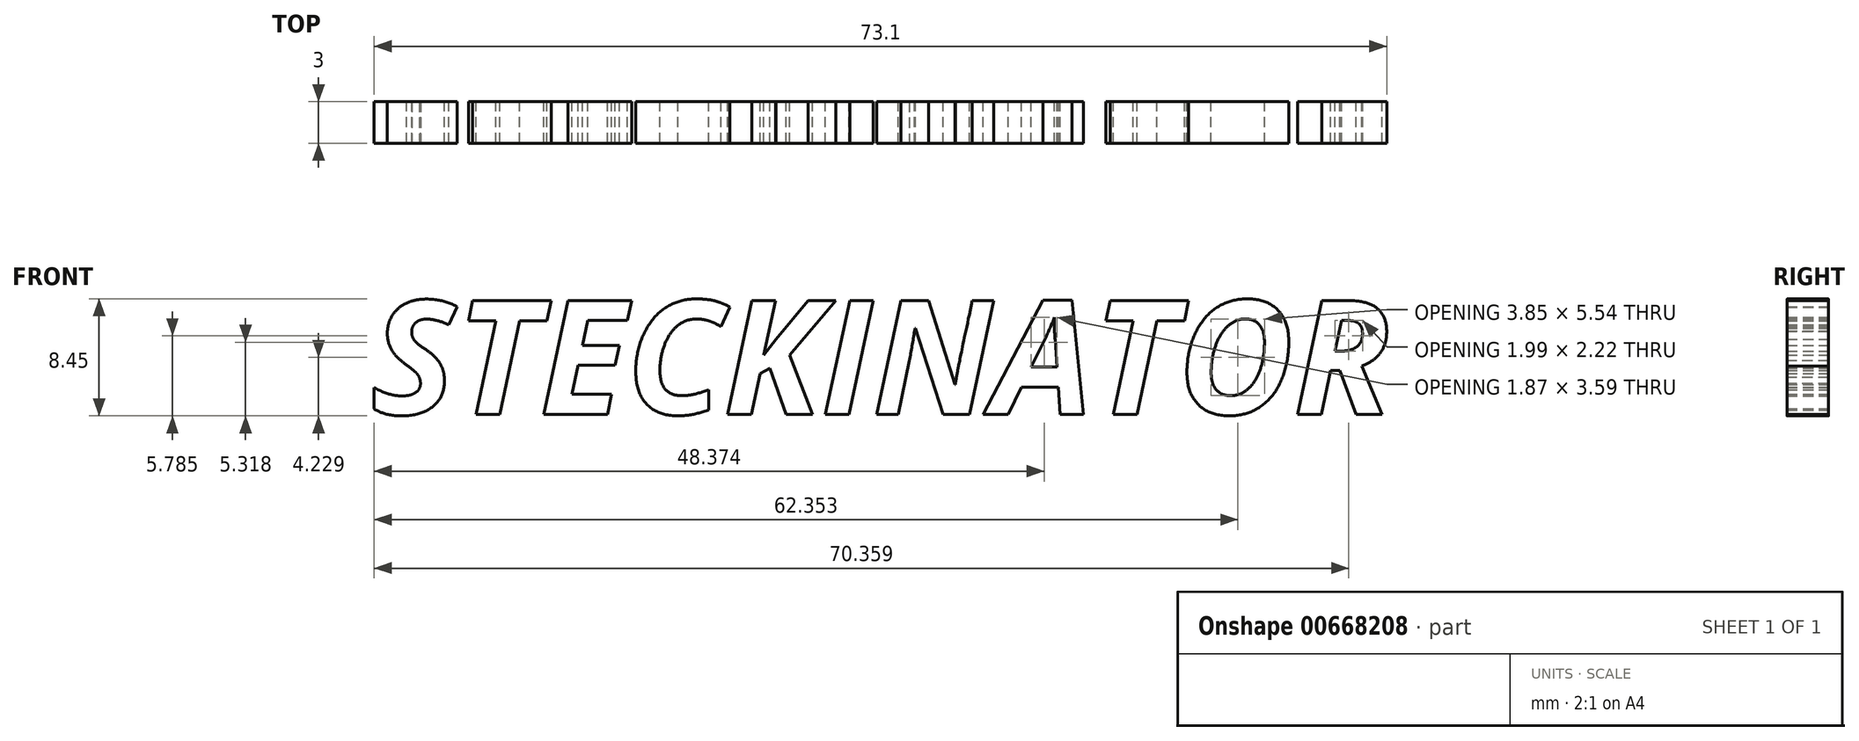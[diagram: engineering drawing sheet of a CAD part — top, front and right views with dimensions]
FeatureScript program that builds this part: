
annotation { "Feature Type Name" : "Feature", "Feature Type Description" : "" }
export const myFeature = defineFeature(function(context is Context, id is Id, definition is map)
    precondition{}
    {
        {
            var Q0;
            Q0=qCreatedBy(makeId("Front.planeOp"),FACE);
            var sketch = newSketch(context, id + "F0", { "sketchPlane" : qUnion([Q0])});
            skText(sketch, "E0", { "text": "STECKINATOR ", "fontName": "OpenSans-BoldItalic.ttf"});
            const initialGuessF0  = {"E0": [-0.0741, 0, 1, 0, 0.00828]};
            skSetInitialGuess(sketch, initialGuessF0);
            skSolve(sketch);
        }
        {
            var Q0;
            Q0 = qSketchRegion(id + "F0", true);
            extrude(context, id + "F1", {"entities" : qUnion([Q0]), "depth" : 3 * mm, "offsetDistance" : 25 * mm});
        }
    });
